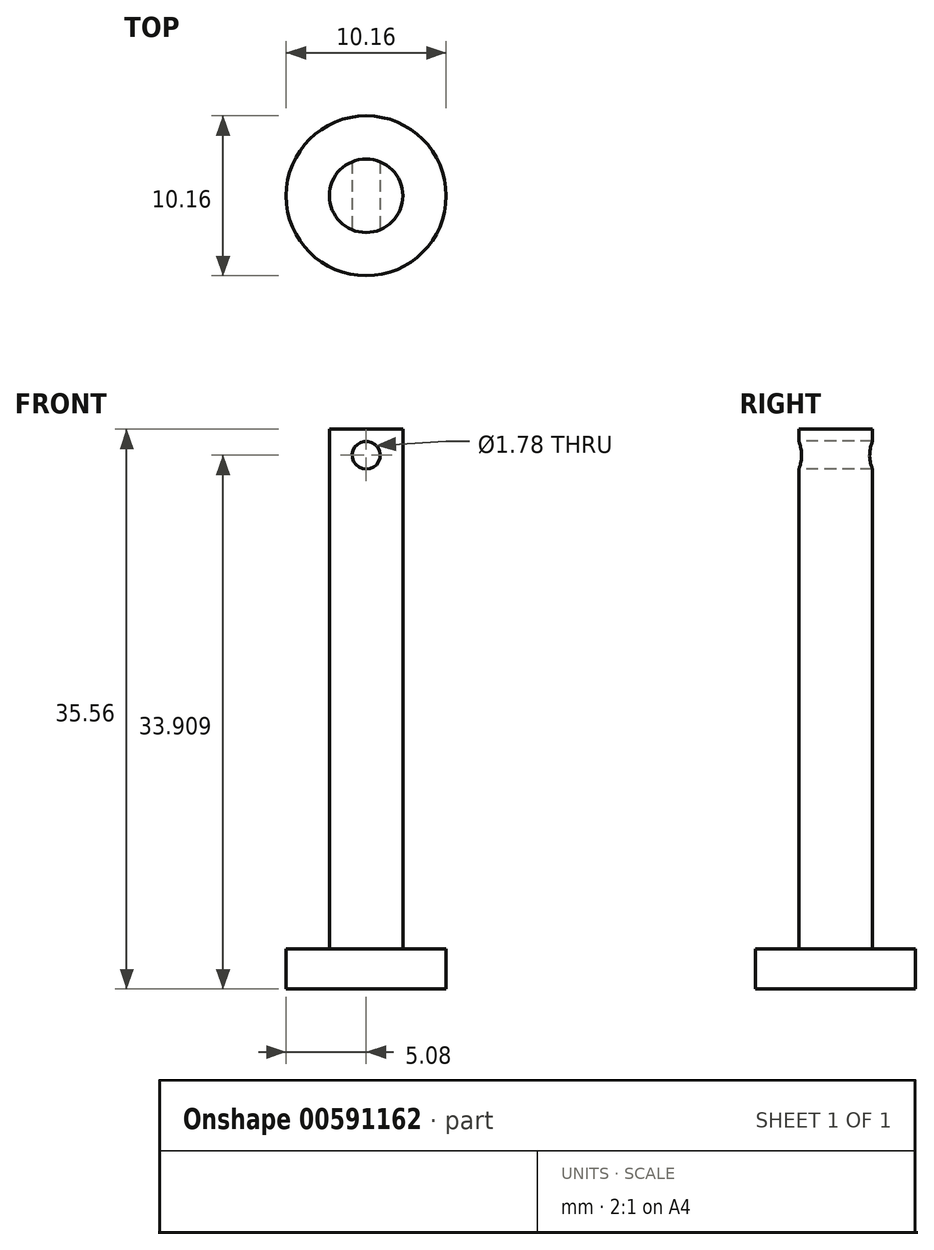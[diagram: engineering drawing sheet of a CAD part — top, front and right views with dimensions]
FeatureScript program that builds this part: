
annotation { "Feature Type Name" : "Feature", "Feature Type Description" : "" }
export const myFeature = defineFeature(function(context is Context, id is Id, definition is map)
    precondition{}
    {
        {
            var Q0;
            Q0=qCreatedBy(makeId("Top.planeOp"),FACE);
            var sketch = newSketch(context, id + "F0", { "sketchPlane" : qUnion([Q0])});
            skCircle(sketch, "E0", {"center": v(0, 0) * mm, "radius": 2.33 * mm});
            skSolve(sketch);
        }
        {
            var Q0;
            Q0=makeQuery(id+"F0.imprint","IMPRINT",FACE,{"disambiguationData":[TD([[makeQuery(id+"F0.imprint","IMPRINT",EDGE,{"derivedFrom":sQuery(id+"F0.wireOp",EDGE,"E0")}),1.0]])]});
            extrude(context, id + "F1", {"entities" : qUnion([Q0]), "depth" : 33.02 * mm, "offsetDistance" : 25.4 * mm});
        }
        {
            var Q0;
            Q0=makeQuery(id+"F1.opExtrude","CAP_FACE",FACE,{"disambiguationData":[OSD([sQuery(id+"F0.wireOp",EDGE,"E0")])],"isStart":true});
            var sketch = newSketch(context, id + "F2", { "sketchPlane" : qUnion([Q0])});
            skCircle(sketch, "E1", {"center": v(0, 0) * mm, "radius": 5.08 * mm});
            skSolve(sketch);
        }
        {
            var Q0;
            Q0=makeQuery(id+"F2.imprint","IMPRINT",FACE,{"disambiguationData":[TD([[makeQuery(id+"F2.imprint","IMPRINT",EDGE,{"derivedFrom":sQuery(id+"F2.wireOp",EDGE,"E1")}),1.0]])]});
            var Q1;
            Q1=makeQuery(id+"F2.imprint","IMPRINT",FACE,{"disambiguationData":[TD([[makeQuery(id+"F2.imprint","IMPRINT",EDGE,{"derivedFrom":makeQuery(id+"F1.opExtrude","CAP_EDGE",EDGE,{"disambiguationData":[OSD([sQuery(id+"F0.wireOp",EDGE,"E0")])],"isStart":true})}),-1.0]])]});
            extrude(context, id + "F3", {"entities" : qUnion([Q0, Q1]), "operationType" : NewBodyOperationType.ADD, "depth" : 2.54 * mm, "offsetDistance" : 25.4 * mm});
        }
        {
            var Q0;
            Q0=qCreatedBy(makeId("Front.planeOp"),FACE);
            var sketch = newSketch(context, id + "F4", { "sketchPlane" : qUnion([Q0])});
            skCircle(sketch, "E2", {"center": v(0, 31.37) * mm, "radius": 0.89 * mm});
            skSolve(sketch);
        }
        {
            var Q0;
            Q0=qSketchRegion(id+"F4",true);
            extrude(context, id + "F5", {"entities" : qUnion([Q0]), "operationType" : NewBodyOperationType.REMOVE, "oppositeDirection" : true, "depth" : 25.4 * mm, "offsetDistance" : 25.4 * mm, "symmetric" : true});
        }
    });
